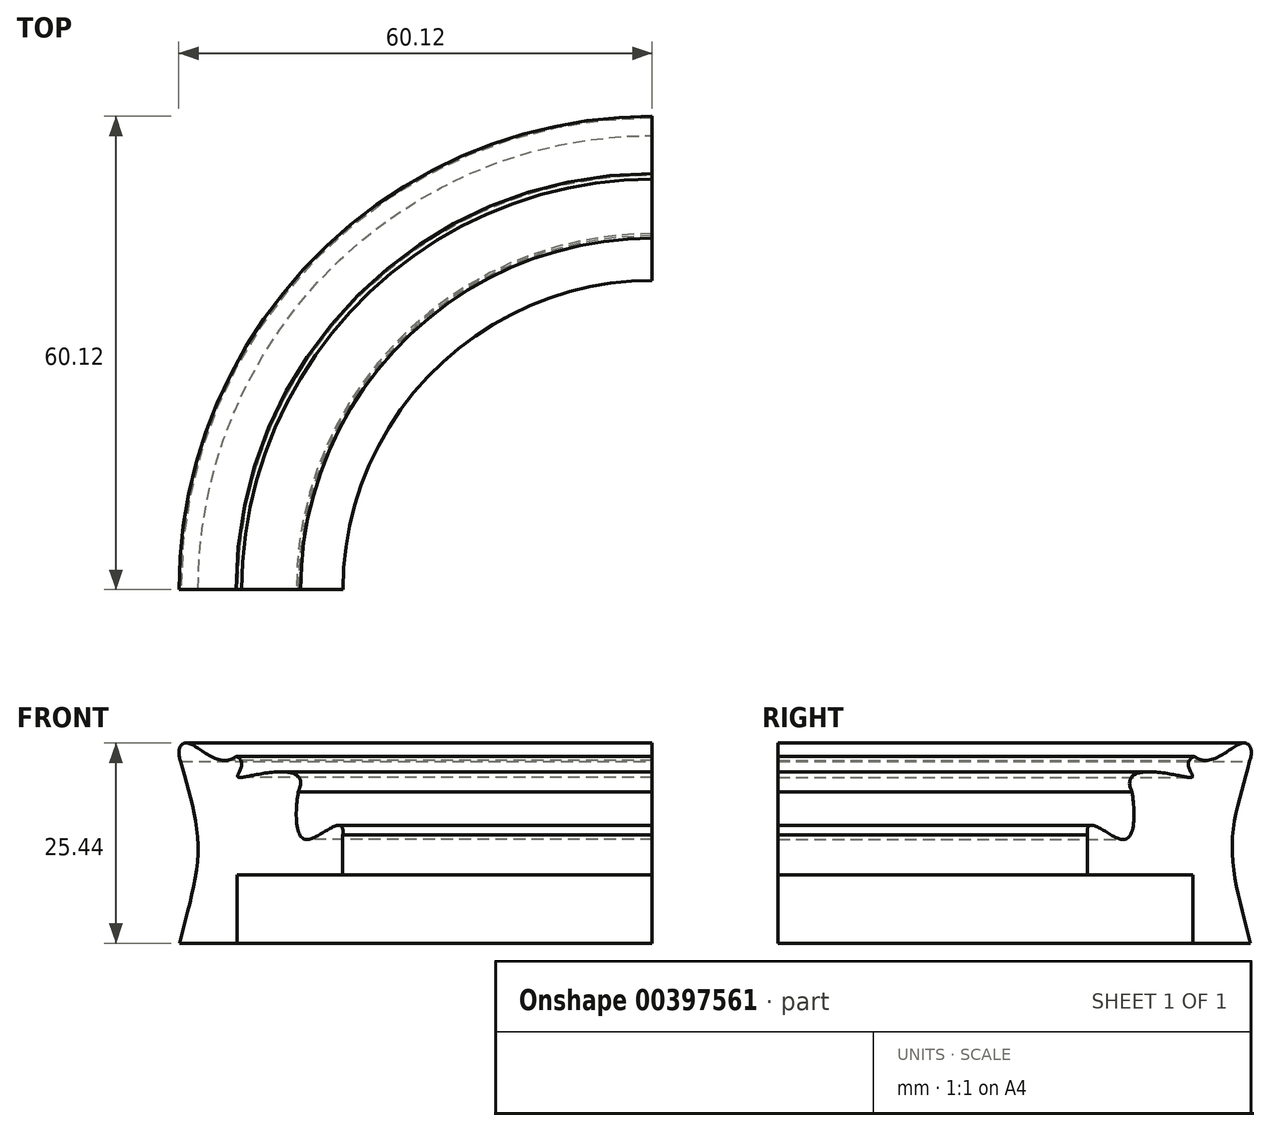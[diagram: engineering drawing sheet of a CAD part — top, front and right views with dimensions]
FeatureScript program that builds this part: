
annotation { "Feature Type Name" : "Feature", "Feature Type Description" : "" }
export const myFeature = defineFeature(function(context is Context, id is Id, definition is map)
    precondition{}
    {
        {
            var Q0;
            Q0=qCreatedBy(makeId("Right.planeOp"),FACE);
            var sketch = newSketch(context, id + "F0", { "sketchPlane" : qUnion([Q0])});
            skLineSegment(sketch, "E0.bottom", {"start": v(0, 0) * mm, "end": v(60, 0) * mm, "construction": true});
            skLineSegment(sketch, "E0.left", {"start": v(0, 0) * mm, "end": v(0, 25.96) * mm, "construction": true});
            skLineSegment(sketch, "E1", {"start": v(39.3, 13.77) * mm, "end": v(39.3, 8.68) * mm});
            skLineSegment(sketch, "E2", {"start": v(39.3, 8.68) * mm, "end": v(52.7, 8.68) * mm});
            skLineSegment(sketch, "E3", {"start": v(52.7, 8.68) * mm, "end": v(52.7, 0) * mm});
            skLineSegment(sketch, "E4", {"start": v(52.7, 0) * mm, "end": v(60, 0) * mm});
            skFitSpline(sketch, "E5", {"points": [v(44.96, 19.2) * mm, v(43.69, 13.18) * mm, v(39.3, 13.77) * mm], "startDerivative": vector(1.81, -12.22) * mm, "endDerivative": vector(2.2, -19.3) * mm});
            skFitSpline(sketch, "E6", {"points": [v(52.86, 23.74) * mm, v(52.65, 21.31) * mm, v(50.22, 21.43) * mm, v(44.96, 19.2) * mm], "startDerivative": vector(-15.48, -7.5) * mm, "endDerivative": vector(10.33, -22.3) * mm});
            skFitSpline(sketch, "E7", {"points": [v(52.86, 23.74) * mm, v(58.98, 25.42) * mm, v(59.87, 23.08) * mm], "startDerivative": vector(11.22, -8.42) * mm, "endDerivative": vector(-4.65, -11.82) * mm});
            skFitSpline(sketch, "E8", {"points": [v(59.87, 23.08) * mm, v(57.68, 12.33) * mm, v(60, 0) * mm], "startDerivative": vector(-4.86, -20.01) * mm, "endDerivative": vector(5.25, -22.72) * mm});
            skSolve(sketch);
        }
        {
            var Q0;
            Q0=makeQuery(id+"F0.imprint","IMPRINT",FACE,{"disambiguationData":[TD([[makeQuery(id+"F0.imprint","IMPRINT",EDGE,{"derivedFrom":sQuery(id+"F0.wireOp",EDGE,"E1")}),1.0]])]});
            var Q1;
            Q1=sQuery(id+"F0.wireOp",EDGE,"E0.left");
            revolve(context, id + "F1", {"entities" : qUnion([Q0]), "axis" : qUnion([Q1]), "revolveType" : RevolveType.ONE_DIRECTION, "angle" : 90 * degree});
        }
    });
